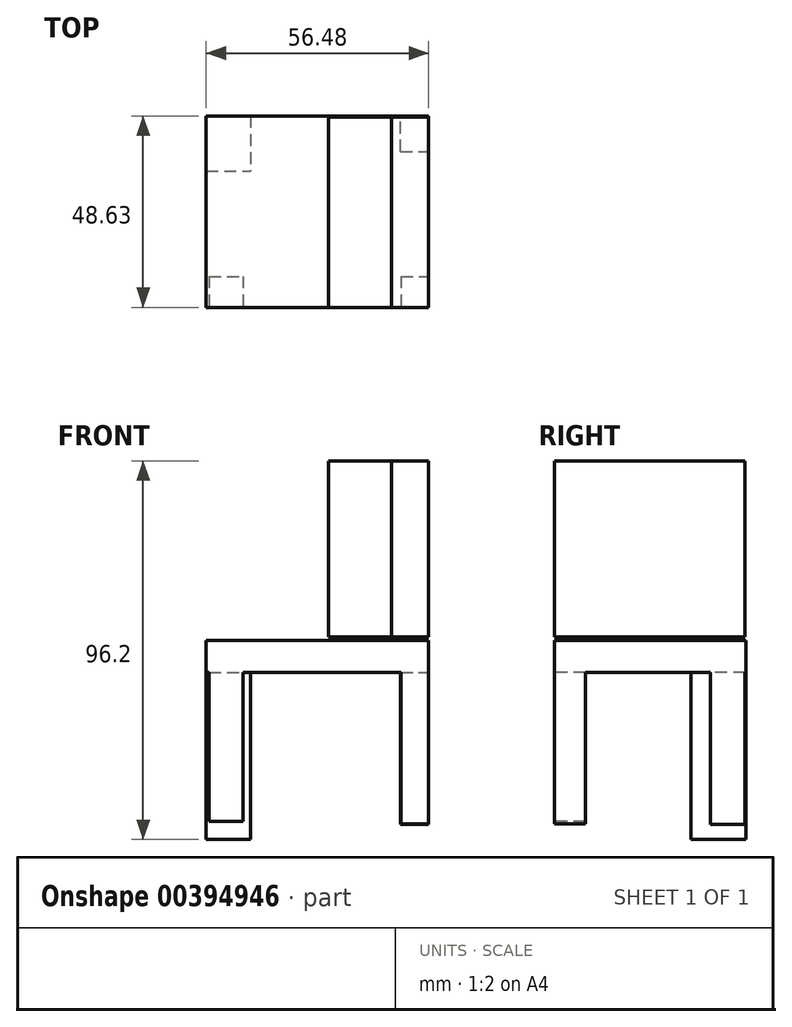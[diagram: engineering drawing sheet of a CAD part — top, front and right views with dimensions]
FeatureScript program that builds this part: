
annotation { "Feature Type Name" : "Feature", "Feature Type Description" : "" }
export const myFeature = defineFeature(function(context is Context, id is Id, definition is map)
    precondition{}
    {
        {
            var Q0;
            Q0=qCreatedBy(makeId("Top.planeOp"),FACE);
            var sketch = newSketch(context, id + "F0", { "sketchPlane" : qUnion([Q0])});
            skLineSegment(sketch, "E0.bottom", {"start": v(0, 0) * mm, "end": v(-56.48, 0) * mm});
            skLineSegment(sketch, "E0.top", {"start": v(0, 48.63) * mm, "end": v(-56.48, 48.63) * mm});
            skLineSegment(sketch, "E0.left", {"start": v(0, 0) * mm, "end": v(0, 48.63) * mm});
            skLineSegment(sketch, "E0.right", {"start": v(-56.48, 0) * mm, "end": v(-56.48, 48.63) * mm});
            skSolve(sketch);
        }
        {
            var Q0;
            Q0 = qSketchRegion(id + "F0", true);
            extrude(context, id + "F1", {"entities" : qUnion([Q0]), "depth" : 8.13 * mm});
        }
        {
            var Q0;
            Q0=qCreatedBy(makeId("Front.planeOp"),FACE);
            var sketch = newSketch(context, id + "F2", { "sketchPlane" : qUnion([Q0])});
            skLineSegment(sketch, "E1.bottom", {"start": v(-55.76, 0) * mm, "end": v(-47.16, 0) * mm});
            skLineSegment(sketch, "E1.top", {"start": v(-55.76, -37.8) * mm, "end": v(-47.16, -37.8) * mm});
            skLineSegment(sketch, "E1.left", {"start": v(-55.76, 0) * mm, "end": v(-55.76, -37.8) * mm});
            skLineSegment(sketch, "E1.right", {"start": v(-47.16, 0) * mm, "end": v(-47.16, -37.8) * mm});
            skLineSegment(sketch, "E2.bottom", {"start": v(-7, 0) * mm, "end": v(0, 0) * mm});
            skLineSegment(sketch, "E2.top", {"start": v(-7, -38.44) * mm, "end": v(0, -38.44) * mm});
            skLineSegment(sketch, "E2.left", {"start": v(-7, 0) * mm, "end": v(-7, -38.44) * mm});
            skLineSegment(sketch, "E2.right", {"start": v(0, 0) * mm, "end": v(0, -38.44) * mm});
            skSolve(sketch);
        }
        {
            var Q0;
            Q0 = qSketchRegion(id + "F2", true);
            extrude(context, id + "F3", {"entities" : qUnion([Q0]), "operationType" : NewBodyOperationType.ADD, "oppositeDirection" : true, "depth" : 7.87 * mm});
        }
        {
            var Q0;
            Q0=qCreatedBy(makeId("Right.planeOp"),FACE);
            var sketch = newSketch(context, id + "F4", { "sketchPlane" : qUnion([Q0])});
            skLineSegment(sketch, "E3.bottom", {"start": v(39.6, 0) * mm, "end": v(48.39, 0) * mm});
            skLineSegment(sketch, "E3.top", {"start": v(39.6, -38.54) * mm, "end": v(48.39, -38.54) * mm});
            skLineSegment(sketch, "E3.left", {"start": v(39.6, 0) * mm, "end": v(39.6, -38.54) * mm});
            skLineSegment(sketch, "E3.right", {"start": v(48.39, 0) * mm, "end": v(48.39, -38.54) * mm});
            skLineSegment(sketch, "E4.bottom", {"start": v(62.59, -18.93) * mm, "end": v(64.62, -18.93) * mm});
            skLineSegment(sketch, "E4.top", {"start": v(62.59, -18.93) * mm, "end": v(64.62, -18.93) * mm});
            skLineSegment(sketch, "E4.left", {"start": v(62.59, -18.93) * mm, "end": v(62.59, -18.93) * mm});
            skLineSegment(sketch, "E4.right", {"start": v(64.62, -18.93) * mm, "end": v(64.62, -18.93) * mm});
            skSolve(sketch);
        }
        {
            var Q0;
            Q0 = qSketchRegion(id + "F4", true);
            extrude(context, id + "F5", {"entities" : qUnion([Q0]), "operationType" : NewBodyOperationType.ADD, "oppositeDirection" : true, "depth" : 7.11 * mm});
        }
        {
            var Q0;
            Q0=makeQuery(id+"F1.opExtrude","CAP_FACE",FACE,{"disambiguationData":[OSD([sQuery(id+"F0.wireOp",EDGE,"E0.bottom"),sQuery(id+"F0.wireOp",EDGE,"E0.top"),sQuery(id+"F0.wireOp",EDGE,"E0.left"),sQuery(id+"F0.wireOp",EDGE,"E0.right")])],"isStart":true});
            var sketch = newSketch(context, id + "F6", { "sketchPlane" : qUnion([Q0])});
            skLineSegment(sketch, "E5.bottom", {"start": v(-56.48, -48.63) * mm, "end": v(-45.21, -48.63) * mm});
            skLineSegment(sketch, "E5.top", {"start": v(-56.48, -34.6) * mm, "end": v(-45.21, -34.6) * mm});
            skLineSegment(sketch, "E5.left", {"start": v(-56.48, -48.63) * mm, "end": v(-56.48, -34.6) * mm});
            skLineSegment(sketch, "E5.right", {"start": v(-45.21, -48.63) * mm, "end": v(-45.21, -34.6) * mm});
            skSolve(sketch);
        }
        {
            var Q0;
            Q0 = qSketchRegion(id + "F6", true);
            extrude(context, id + "F7", {"entities" : qUnion([Q0]), "operationType" : NewBodyOperationType.ADD, "depth" : 42.42 * mm});
        }
        {
            var Q0;
            Q0=qCreatedBy(makeId("Right.planeOp"),FACE);
            var sketch = newSketch(context, id + "F8", { "sketchPlane" : qUnion([Q0])});
            skLineSegment(sketch, "E6.bottom", {"start": v(0, 9.04) * mm, "end": v(48.4, 9.04) * mm});
            skLineSegment(sketch, "E6.top", {"start": v(0, 53.78) * mm, "end": v(48.4, 53.78) * mm});
            skLineSegment(sketch, "E6.left", {"start": v(0, 9.04) * mm, "end": v(0, 53.78) * mm});
            skLineSegment(sketch, "E6.right", {"start": v(48.4, 9.04) * mm, "end": v(48.4, 53.78) * mm});
            skSolve(sketch);
        }
        {
            var Q0;
            Q0=makeQuery(id+"F8.imprint","IMPRINT",FACE,{"disambiguationData":[TD([[makeQuery(id+"F8.imprint","IMPRINT",EDGE,{"derivedFrom":sQuery(id+"F8.wireOp",EDGE,"E6.bottom")}),1.0]])]});
            extrude(context, id + "F9", {"entities" : qUnion([Q0]), "operationType" : NewBodyOperationType.ADD, "oppositeDirection" : true, "depth" : 25.4 * mm});
        }
        {
            var Q0;
            Q0 = qSketchRegion(id + "F8", true);
            extrude(context, id + "F10", {"entities" : qUnion([Q0]), "oppositeDirection" : true, "depth" : 9.4 * mm});
        }
    });
